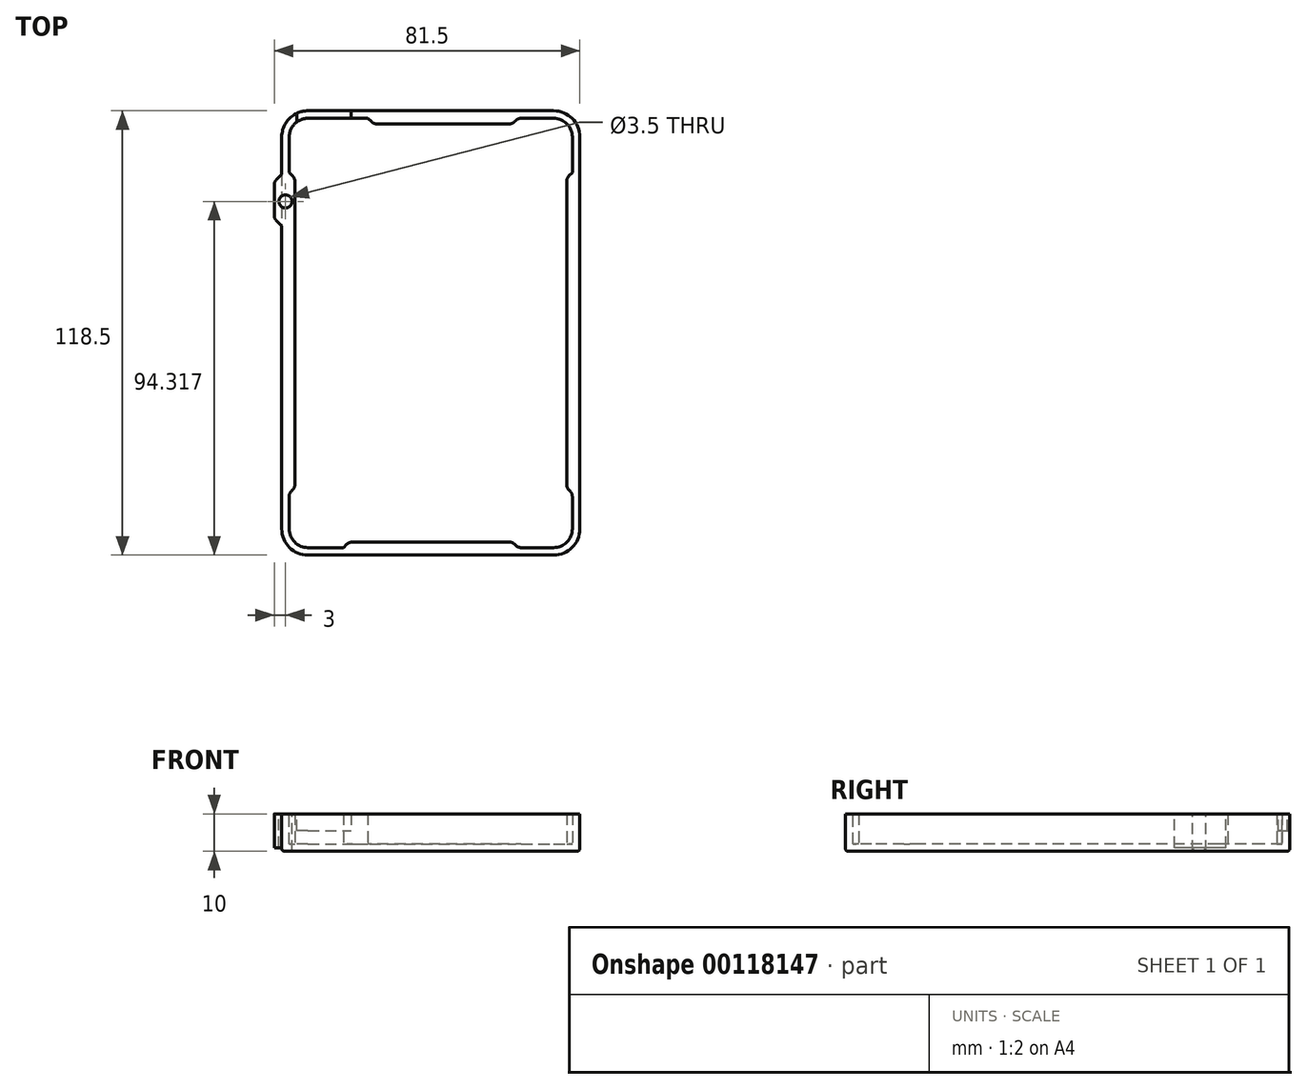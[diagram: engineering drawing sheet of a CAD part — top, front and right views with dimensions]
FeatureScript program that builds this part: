
annotation { "Feature Type Name" : "Feature", "Feature Type Description" : "" }
export const myFeature = defineFeature(function(context is Context, id is Id, definition is map)
    precondition{}
    {
        {
            var Q0;
            Q0=qCreatedBy(makeId("Top.planeOp"),FACE);
            var sketch = newSketch(context, id + "F0", { "sketchPlane" : qUnion([Q0])});
            skLineSegment(sketch, "E0.bottom", {"start": v(-39.75, 118.5) * mm, "end": v(39.75, 118.5) * mm});
            skLineSegment(sketch, "E0.top", {"start": v(-39.75, 0) * mm, "end": v(39.75, 0) * mm});
            skLineSegment(sketch, "E0.left", {"start": v(-39.75, 118.5) * mm, "end": v(-39.75, 0) * mm});
            skLineSegment(sketch, "E0.right", {"start": v(39.75, 118.5) * mm, "end": v(39.75, 0) * mm});
            skSolve(sketch);
        }
        {
            var Q0;
            Q0=makeQuery(id+"F0.imprint","IMPRINT",FACE,{"disambiguationData":[TD([[makeQuery(id+"F0.imprint","IMPRINT",EDGE,{"derivedFrom":sQuery(id+"F0.wireOp",EDGE,"E0.bottom")}),-1.0]])]});
            extrude(context, id + "F1", {"entities" : qUnion([Q0]), "depth" : 10 * mm});
        }
        {
            var Q0;
            Q0=makeQuery(id+"F1.opExtrude","SWEPT_FACE",FACE,{"disambiguationData":[OSD([sQuery(id+"F0.wireOp",EDGE,"E0.bottom")])]});
            var sketch = newSketch(context, id + "F2", { "sketchPlane" : qUnion([Q0])});
            skLineSegment(sketch, "E1.bottom", {"start": v(35.75, 10) * mm, "end": v(21.25, 10) * mm});
            skLineSegment(sketch, "E1.top", {"start": v(35.75, 5.5) * mm, "end": v(21.25, 5.5) * mm});
            skLineSegment(sketch, "E1.left", {"start": v(35.75, 10) * mm, "end": v(35.75, 5.5) * mm});
            skLineSegment(sketch, "E1.right", {"start": v(21.25, 10) * mm, "end": v(21.25, 5.5) * mm});
            skSolve(sketch);
        }
        {
            var Q0;
            Q0=makeQuery(id+"F1.opExtrude","SWEPT_EDGE",EDGE,{"disambiguationData":[OSD([sQuery(id+"F0.wireOp",EDGE,"E0.bottom"),sQuery(id+"F0.wireOp",EDGE,"E0.left")])]});
            var Q1;
            Q1=makeQuery(id+"F1.opExtrude","SWEPT_EDGE",EDGE,{"disambiguationData":[OSD([sQuery(id+"F0.wireOp",EDGE,"E0.top"),sQuery(id+"F0.wireOp",EDGE,"E0.left")])]});
            var Q2;
            Q2=makeQuery(id+"F1.opExtrude","SWEPT_EDGE",EDGE,{"disambiguationData":[OSD([sQuery(id+"F0.wireOp",EDGE,"E0.top"),sQuery(id+"F0.wireOp",EDGE,"E0.right")])]});
            var Q3;
            Q3=makeQuery(id+"F1.opExtrude","SWEPT_EDGE",EDGE,{"disambiguationData":[OSD([sQuery(id+"F0.wireOp",EDGE,"E0.bottom"),sQuery(id+"F0.wireOp",EDGE,"E0.right")])]});
            fillet(context, id + "F3", {"entities" : qUnion([Q0, Q1, Q2, Q3]), "radius" : 7 * mm, "tangentPropagation" : true, "allowEdgeOverflow" : false});
        }
        {
            var Q0;
            Q0=makeQuery(id+"F1.opExtrude","CAP_FACE",FACE,{"disambiguationData":[OSD([sQuery(id+"F0.wireOp",EDGE,"E0.bottom"),sQuery(id+"F0.wireOp",EDGE,"E0.top"),sQuery(id+"F0.wireOp",EDGE,"E0.left"),sQuery(id+"F0.wireOp",EDGE,"E0.right")])],"isStart":false});
            var sketch = newSketch(context, id + "F4", { "sketchPlane" : qUnion([Q0])});
            skLineSegment(sketch, "E2.bottom", {"start": v(-32.75, 116.5) * mm, "end": v(32.75, 116.5) * mm});
            skLineSegment(sketch, "E2.top", {"start": v(-32.75, 2) * mm, "end": v(32.75, 2) * mm});
            skLineSegment(sketch, "E2.left", {"start": v(-37.75, 111.5) * mm, "end": v(-37.75, 7) * mm});
            skLineSegment(sketch, "E2.right", {"start": v(37.75, 111.5) * mm, "end": v(37.75, 7) * mm});
            skPoint(sketch, "E3.visualSharp", {"position": v(-37.75, 2) * mm});
            skArc(sketch, "E3.filletArc", {"start": v(-37.75, 7) * mm, "mid": v(-36.29, 3.46) * mm, "end": v(-32.75, 2) * mm});
            skPoint(sketch, "E4.visualSharp", {"position": v(37.75, 2) * mm});
            skArc(sketch, "E4.filletArc", {"start": v(32.75, 2) * mm, "mid": v(36.29, 3.46) * mm, "end": v(37.75, 7) * mm});
            skPoint(sketch, "E5.visualSharp", {"position": v(-37.75, 116.5) * mm});
            skArc(sketch, "E5.filletArc", {"start": v(-32.75, 116.5) * mm, "mid": v(-36.29, 115.04) * mm, "end": v(-37.75, 111.5) * mm});
            skPoint(sketch, "E6.visualSharp", {"position": v(37.75, 116.5) * mm});
            skArc(sketch, "E6.filletArc", {"start": v(37.75, 111.5) * mm, "mid": v(36.29, 115.04) * mm, "end": v(32.75, 116.5) * mm});
            skSolve(sketch);
        }
        {
            var Q0;
            Q0=makeQuery(id+"F4.imprint","IMPRINT",FACE,{"disambiguationData":[TD([[makeQuery(id+"F4.imprint","IMPRINT",EDGE,{"derivedFrom":sQuery(id+"F4.wireOp",EDGE,"E2.bottom")}),-1.0]])]});
            extrude(context, id + "F5", {"entities" : qUnion([Q0]), "operationType" : NewBodyOperationType.REMOVE, "oppositeDirection" : true, "depth" : 3.5 * mm});
        }
        {
            var Q0;
            Q0=makeQuery(id+"F1.opExtrude","CAP_FACE",FACE,{"disambiguationData":[OSD([sQuery(id+"F0.wireOp",EDGE,"E0.bottom"),sQuery(id+"F0.wireOp",EDGE,"E0.top"),sQuery(id+"F0.wireOp",EDGE,"E0.left"),sQuery(id+"F0.wireOp",EDGE,"E0.right")])],"isStart":true});
            fillet(context, id + "F6", {"entities" : qUnion([Q0]), "radius" : 0.8 * mm, "tangentPropagation" : true, "allowEdgeOverflow" : false});
        }
        {
            var Q0;
            Q0=makeQuery(id+"F5.boolean.opBoolean","COPY",FACE,{"derivedFrom":makeQuery(id+"F5.opExtrude","CAP_FACE",FACE,{"disambiguationData":[OSD([sQuery(id+"F4.wireOp",EDGE,"E2.bottom"),sQuery(id+"F4.wireOp",EDGE,"E2.top"),sQuery(id+"F4.wireOp",EDGE,"E2.left"),sQuery(id+"F4.wireOp",EDGE,"E2.right"),sQuery(id+"F4.wireOp",EDGE,"E3.filletArc"),sQuery(id+"F4.wireOp",EDGE,"E4.filletArc"),sQuery(id+"F4.wireOp",EDGE,"E5.filletArc"),sQuery(id+"F4.wireOp",EDGE,"E6.filletArc")])],"isStart":false})});
            var sketch = newSketch(context, id + "F7", { "sketchPlane" : qUnion([Q0])});
            skLineSegment(sketch, "E7", {"start": v(-37.75, 102) * mm, "end": v(-36.25, 100.5) * mm});
            skLineSegment(sketch, "E8", {"start": v(-36.25, 100.5) * mm, "end": v(-36.25, 18) * mm});
            skLineSegment(sketch, "E9", {"start": v(-36.25, 18) * mm, "end": v(-37.75, 16.5) * mm});
            skLineSegment(sketch, "E10", {"start": v(-37.75, 16.5) * mm, "end": v(-37.75, 102) * mm});
            skLineSegment(sketch, "E11", {"start": v(37.75, 102) * mm, "end": v(36.25, 100.5) * mm});
            skLineSegment(sketch, "E12", {"start": v(36.25, 100.5) * mm, "end": v(36.25, 18) * mm});
            skLineSegment(sketch, "E13", {"start": v(36.25, 18) * mm, "end": v(37.75, 16.5) * mm});
            skLineSegment(sketch, "E14", {"start": v(37.75, 16.5) * mm, "end": v(37.75, 102) * mm});
            skLineSegment(sketch, "E15", {"start": v(-23.25, 2) * mm, "end": v(-21.75, 3.5) * mm});
            skLineSegment(sketch, "E16", {"start": v(-21.75, 3.5) * mm, "end": v(21.75, 3.5) * mm});
            skLineSegment(sketch, "E17", {"start": v(21.75, 3.5) * mm, "end": v(23.25, 2) * mm});
            skLineSegment(sketch, "E18", {"start": v(23.25, 2) * mm, "end": v(-23.25, 2) * mm});
            skLineSegment(sketch, "E19", {"start": v(23.25, 116.5) * mm, "end": v(21.75, 115) * mm});
            skLineSegment(sketch, "E20", {"start": v(21.75, 115) * mm, "end": v(-15.25, 115) * mm});
            skLineSegment(sketch, "E21", {"start": v(-15.25, 115) * mm, "end": v(-16.75, 116.5) * mm});
            skLineSegment(sketch, "E22", {"start": v(-16.75, 116.5) * mm, "end": v(23.25, 116.5) * mm});
            skSolve(sketch);
        }
        {
            var Q0;
            Q0=makeQuery(id+"F7.imprint","IMPRINT",FACE,{"disambiguationData":[TD([[makeQuery(id+"F7.imprint","IMPRINT",EDGE,{"derivedFrom":sQuery(id+"F7.wireOp",EDGE,"E7")}),-1.0]])]});
            var Q1;
            Q1=makeQuery(id+"F7.imprint","IMPRINT",FACE,{"disambiguationData":[TD([[makeQuery(id+"F7.imprint","IMPRINT",EDGE,{"derivedFrom":sQuery(id+"F7.wireOp",EDGE,"E11")}),1.0]])]});
            var Q2;
            Q2=makeQuery(id+"F7.imprint","IMPRINT",FACE,{"disambiguationData":[TD([[makeQuery(id+"F7.imprint","IMPRINT",EDGE,{"derivedFrom":sQuery(id+"F7.wireOp",EDGE,"E15")}),-1.0]])]});
            var Q3;
            Q3=makeQuery(id+"F7.imprint","IMPRINT",FACE,{"disambiguationData":[TD([[makeQuery(id+"F7.imprint","IMPRINT",EDGE,{"derivedFrom":sQuery(id+"F7.wireOp",EDGE,"E19")}),-1.0]])]});
            extrude(context, id + "F8", {"entities" : qUnion([Q0, Q1, Q2, Q3]), "operationType" : NewBodyOperationType.ADD, "depth" : 3.5 * mm});
        }
        {
            var Q0;
            Q0=makeQuery(id+"F8.opExtrude","SWEPT_EDGE",EDGE,{"disambiguationData":[OSD([sQuery(id+"F4.wireOp",EDGE,"E2.left"),sQuery(id+"F7.wireOp",EDGE,"E7"),sQuery(id+"F7.wireOp",EDGE,"E10")])]});
            var Q1;
            Q1=makeQuery(id+"F8.opExtrude","SWEPT_EDGE",EDGE,{"disambiguationData":[OSD([sQuery(id+"F7.wireOp",EDGE,"E7"),sQuery(id+"F7.wireOp",EDGE,"E8")])]});
            var Q2;
            Q2=makeQuery(id+"F8.opExtrude","SWEPT_EDGE",EDGE,{"disambiguationData":[OSD([sQuery(id+"F4.wireOp",EDGE,"E2.left"),sQuery(id+"F7.wireOp",EDGE,"E9"),sQuery(id+"F7.wireOp",EDGE,"E10")])]});
            var Q3;
            Q3=makeQuery(id+"F8.opExtrude","SWEPT_EDGE",EDGE,{"disambiguationData":[OSD([sQuery(id+"F7.wireOp",EDGE,"E8"),sQuery(id+"F7.wireOp",EDGE,"E9")])]});
            var Q4;
            Q4=makeQuery(id+"F8.opExtrude","SWEPT_EDGE",EDGE,{"disambiguationData":[OSD([sQuery(id+"F7.wireOp",EDGE,"E11"),sQuery(id+"F7.wireOp",EDGE,"E12")])]});
            var Q5;
            Q5=makeQuery(id+"F8.opExtrude","SWEPT_EDGE",EDGE,{"disambiguationData":[OSD([sQuery(id+"F4.wireOp",EDGE,"E2.right"),sQuery(id+"F7.wireOp",EDGE,"E11"),sQuery(id+"F7.wireOp",EDGE,"E14")])]});
            var Q6;
            Q6=makeQuery(id+"F8.opExtrude","SWEPT_EDGE",EDGE,{"disambiguationData":[OSD([sQuery(id+"F7.wireOp",EDGE,"E12"),sQuery(id+"F7.wireOp",EDGE,"E13")])]});
            var Q7;
            Q7=makeQuery(id+"F8.opExtrude","SWEPT_EDGE",EDGE,{"disambiguationData":[OSD([sQuery(id+"F4.wireOp",EDGE,"E2.right"),sQuery(id+"F7.wireOp",EDGE,"E13"),sQuery(id+"F7.wireOp",EDGE,"E14")])]});
            var Q8;
            Q8=makeQuery(id+"F8.opExtrude","SWEPT_EDGE",EDGE,{"disambiguationData":[OSD([sQuery(id+"F4.wireOp",EDGE,"E2.top"),sQuery(id+"F7.wireOp",EDGE,"E17"),sQuery(id+"F7.wireOp",EDGE,"E18")])]});
            var Q9;
            Q9=makeQuery(id+"F8.opExtrude","SWEPT_EDGE",EDGE,{"disambiguationData":[OSD([sQuery(id+"F7.wireOp",EDGE,"E16"),sQuery(id+"F7.wireOp",EDGE,"E17")])]});
            var Q10;
            Q10=makeQuery(id+"F8.opExtrude","SWEPT_EDGE",EDGE,{"disambiguationData":[OSD([sQuery(id+"F4.wireOp",EDGE,"E2.top"),sQuery(id+"F7.wireOp",EDGE,"E15"),sQuery(id+"F7.wireOp",EDGE,"E18")])]});
            var Q11;
            Q11=makeQuery(id+"F8.opExtrude","SWEPT_EDGE",EDGE,{"disambiguationData":[OSD([sQuery(id+"F7.wireOp",EDGE,"E15"),sQuery(id+"F7.wireOp",EDGE,"E16")])]});
            var Q12;
            Q12=makeQuery(id+"F8.opExtrude","SWEPT_EDGE",EDGE,{"disambiguationData":[OSD([sQuery(id+"F4.wireOp",EDGE,"E2.bottom"),sQuery(id+"F7.wireOp",EDGE,"E21"),sQuery(id+"F7.wireOp",EDGE,"E22")])]});
            var Q13;
            Q13=makeQuery(id+"F8.opExtrude","SWEPT_EDGE",EDGE,{"disambiguationData":[OSD([sQuery(id+"F7.wireOp",EDGE,"E20"),sQuery(id+"F7.wireOp",EDGE,"E21")])]});
            var Q14;
            Q14=makeQuery(id+"F8.opExtrude","SWEPT_EDGE",EDGE,{"disambiguationData":[OSD([sQuery(id+"F7.wireOp",EDGE,"E19"),sQuery(id+"F7.wireOp",EDGE,"E20")])]});
            var Q15;
            Q15=makeQuery(id+"F8.opExtrude","SWEPT_EDGE",EDGE,{"disambiguationData":[OSD([sQuery(id+"F4.wireOp",EDGE,"E2.bottom"),sQuery(id+"F7.wireOp",EDGE,"E19"),sQuery(id+"F7.wireOp",EDGE,"E22")])]});
            fillet(context, id + "F9", {"entities" : qUnion([Q0, Q1, Q2, Q3, Q4, Q5, Q6, Q7, Q8, Q9, Q10, Q11, Q12, Q13, Q14, Q15]), "radius" : 2 * mm, "tangentPropagation" : true, "allowEdgeOverflow" : false});
        }
        {
            var Q0;
            Q0=makeQuery(id+"F5.boolean.opBoolean","COPY",FACE,{"derivedFrom":makeQuery(id+"F5.opExtrude","CAP_FACE",FACE,{"disambiguationData":[OSD([sQuery(id+"F4.wireOp",EDGE,"E2.bottom"),sQuery(id+"F4.wireOp",EDGE,"E2.top"),sQuery(id+"F4.wireOp",EDGE,"E2.left"),sQuery(id+"F4.wireOp",EDGE,"E2.right"),sQuery(id+"F4.wireOp",EDGE,"E3.filletArc"),sQuery(id+"F4.wireOp",EDGE,"E4.filletArc"),sQuery(id+"F4.wireOp",EDGE,"E5.filletArc"),sQuery(id+"F4.wireOp",EDGE,"E6.filletArc")])],"isStart":false})});
            extrude(context, id + "F10", {"entities" : qUnion([Q0]), "operationType" : NewBodyOperationType.REMOVE, "oppositeDirection" : true, "depth" : 4.5 * mm});
        }
        {
            var Q0;
            Q0=makeQuery(id+"F2.imprint","IMPRINT",FACE,{"disambiguationData":[TD([[makeQuery(id+"F2.imprint","IMPRINT",EDGE,{"derivedFrom":sQuery(id+"F2.wireOp",EDGE,"E1.bottom")}),1.0]])]});
            extrude(context, id + "F11", {"entities" : qUnion([Q0]), "operationType" : NewBodyOperationType.REMOVE, "oppositeDirection" : true, "depth" : 4 * mm});
        }
        {
            var Q0;
            Q0=makeQuery(id+"F8.boolean.opBoolean","MERGE",FACE,{"derivedFrom":[makeQuery(id+"F1.opExtrude","CAP_FACE",FACE,{"disambiguationData":[OSD([sQuery(id+"F0.wireOp",EDGE,"E0.bottom"),sQuery(id+"F0.wireOp",EDGE,"E0.top"),sQuery(id+"F0.wireOp",EDGE,"E0.left"),sQuery(id+"F0.wireOp",EDGE,"E0.right")])],"isStart":false}),makeQuery(id+"F8.opExtrude","CAP_FACE",FACE,{"disambiguationData":[OSD([sQuery(id+"F7.wireOp",EDGE,"E7"),sQuery(id+"F7.wireOp",EDGE,"E8"),sQuery(id+"F7.wireOp",EDGE,"E9"),sQuery(id+"F7.wireOp",EDGE,"E10")])],"isStart":false}),makeQuery(id+"F8.opExtrude","CAP_FACE",FACE,{"disambiguationData":[OSD([sQuery(id+"F7.wireOp",EDGE,"E11"),sQuery(id+"F7.wireOp",EDGE,"E12"),sQuery(id+"F7.wireOp",EDGE,"E13"),sQuery(id+"F7.wireOp",EDGE,"E14")])],"isStart":false})]});
            var sketch = newSketch(context, id + "F12", { "sketchPlane" : qUnion([Q0])});
            skCircle(sketch, "E23", {"center": v(-38.75, 94.32) * mm, "radius": 1.75 * mm});
            skLineSegment(sketch, "E24", {"start": v(-39.75, 101.5) * mm, "end": v(-41.75, 99.5) * mm});
            skLineSegment(sketch, "E25", {"start": v(-41.75, 99.5) * mm, "end": v(-41.75, 89.77) * mm});
            skLineSegment(sketch, "E26", {"start": v(-41.75, 89.77) * mm, "end": v(-39.75, 87.77) * mm});
            skLineSegment(sketch, "E27", {"start": v(-39.75, 87.77) * mm, "end": v(-39.75, 101.5) * mm});
            skSolve(sketch);
        }
        {
            var Q0;
            Q0=makeQuery(id+"F12.imprint","IMPRINT",FACE,{"disambiguationData":[TD([[makeQuery(id+"F12.imprint","IMPRINT",EDGE,{"derivedFrom":sQuery(id+"F12.wireOp",EDGE,"E24")}),1.0]])]});
            extrude(context, id + "F13", {"entities" : qUnion([Q0]), "operationType" : NewBodyOperationType.ADD, "oppositeDirection" : true, "depth" : 9 * mm});
        }
        {
            var Q0;
            Q0=makeQuery(id+"F12.imprint","IMPRINT",FACE,{"disambiguationData":[TD([[makeQuery(id+"F12.imprint","IMPRINT",EDGE,{"derivedFrom":sQuery(id+"F12.wireOp",EDGE,"E23")}),1.0]])]});
            extrude(context, id + "F14", {"entities" : qUnion([Q0]), "operationType" : NewBodyOperationType.REMOVE, "oppositeDirection" : true, "depth" : 25 * mm});
        }
        {
            var Q0;
            Q0=makeQuery(id+"F13.opExtrude","SWEPT_EDGE",EDGE,{"disambiguationData":[OSD([sQuery(id+"F12.wireOp",EDGE,"E24"),sQuery(id+"F12.wireOp",EDGE,"E25")])]});
            var Q1;
            Q1=makeQuery(id+"F13.opExtrude","SWEPT_EDGE",EDGE,{"disambiguationData":[OSD([sQuery(id+"F0.wireOp",EDGE,"E0.left"),sQuery(id+"F12.wireOp",EDGE,"E24"),sQuery(id+"F12.wireOp",EDGE,"E27")])]});
            var Q2;
            Q2=makeQuery(id+"F13.opExtrude","SWEPT_EDGE",EDGE,{"disambiguationData":[OSD([sQuery(id+"F12.wireOp",EDGE,"E25"),sQuery(id+"F12.wireOp",EDGE,"E26")])]});
            var Q3;
            Q3=makeQuery(id+"F13.opExtrude","SWEPT_EDGE",EDGE,{"disambiguationData":[OSD([sQuery(id+"F0.wireOp",EDGE,"E0.left"),sQuery(id+"F12.wireOp",EDGE,"E26"),sQuery(id+"F12.wireOp",EDGE,"E27")])]});
            fillet(context, id + "F15", {"entities" : qUnion([Q0, Q1, Q2, Q3]), "radius" : 2 * mm, "tangentPropagation" : true, "allowEdgeOverflow" : false});
        }
    });
